# Revit family: P190780JX-189c_JWD3027EX_WoodPanel_JA_Cooking_Warming_Drawers
name_source: partatom
category: Specialty Equipment
units: mm (PartAtom-declared; Revit-internal decimal feet)

## family parameters
Always vertical = Yes
Cut with Voids When Loaded = No
Enable Cutting in Views = No
Maintain Annotation Orientation = No
Part Type = Normal
Room Calculation Point = No
Round Connector Dimension = Use Diameter
Shared = No
Work Plane-Based = No

## types (1)
- JWD3027EX
    Amps = 15 A
    Body Material = ARCAT - Metal - Steel - Stainless
    Clearance Material = ARCAT - Clearance
    Default Elevation = 0"
    Depth = 25"
    Description = Panel-Ready 27” Warming Drawer
Tiroir-réchaud, 27 po
    Dimension Guide = http://access.whirlpool.com Guide&sku=JWD3027EX&language=EN
http://access.whirlpool.com Guide&sku=JWD3027EX&language=EN
    Door Panel Material = ARCAT - Thermal - Wood Fiber Cover Board
    Family Name = WARMING DRAWERS - 27"
    Feature 1 = Sensor Temperature Control
Commande de température par capteur
    Feature 2 = Slow Roast Function
Fonction de rôtissage lent
    Feature 3 = Bread Proofing Function
Fonction de levage du pain
    Handle Material = ARCAT - Metal - Steel - Gray
    Height = 10 1/4"
    Installation-Fabrication = http://access.whirlpool.com Instruction&sku=JWD3027EX&language=EN
http://access.whirlpool.com Instruction&sku=JWD3027EX&language=FR
    Manufacturer = JennAir
    Model = JWD3027EX
    Voltage = 120 V
    Width = 26 3/4"

## geometry (parser evidence)
native form markers: Sweep x4
no freeform markers — native parametric forms only
